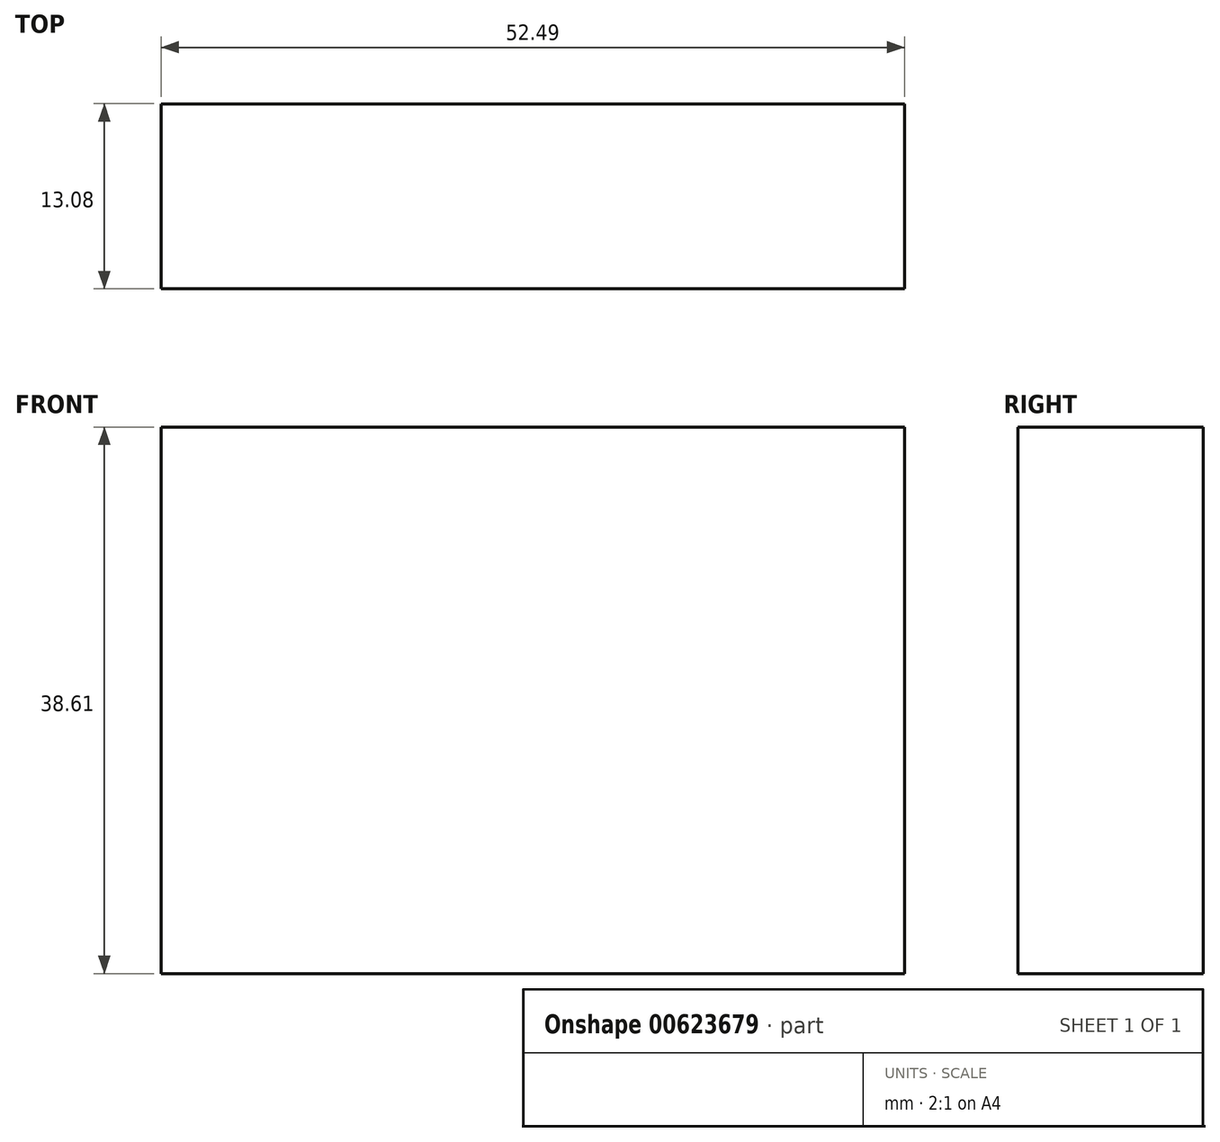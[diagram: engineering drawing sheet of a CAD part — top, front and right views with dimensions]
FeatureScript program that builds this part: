
annotation { "Feature Type Name" : "Feature", "Feature Type Description" : "" }
export const myFeature = defineFeature(function(context is Context, id is Id, definition is map)
    precondition{}
    {
        {
            var Q0;
            Q0=qCreatedBy(makeId("Top.planeOp"),FACE);
            var sketch = newSketch(context, id + "F0", { "sketchPlane" : qUnion([Q0])});
            skLineSegment(sketch, "E0.bottom", {"start": v(-52.49, 12.83) * mm, "end": v(0, 12.83) * mm});
            skLineSegment(sketch, "E0.top", {"start": v(-52.49, 25.9) * mm, "end": v(0, 25.9) * mm});
            skLineSegment(sketch, "E0.left", {"start": v(-52.49, 12.83) * mm, "end": v(-52.49, 25.9) * mm});
            skLineSegment(sketch, "E0.right", {"start": v(0, 12.83) * mm, "end": v(0, 25.9) * mm});
            skSolve(sketch);
        }
        {
            var Q0;
            Q0 = qSketchRegion(id + "F0", true);
            extrude(context, id + "F1", {"entities" : qUnion([Q0]), "depth" : 38.6 * mm, "offsetDistance" : 25.4 * mm});
        }
    });
